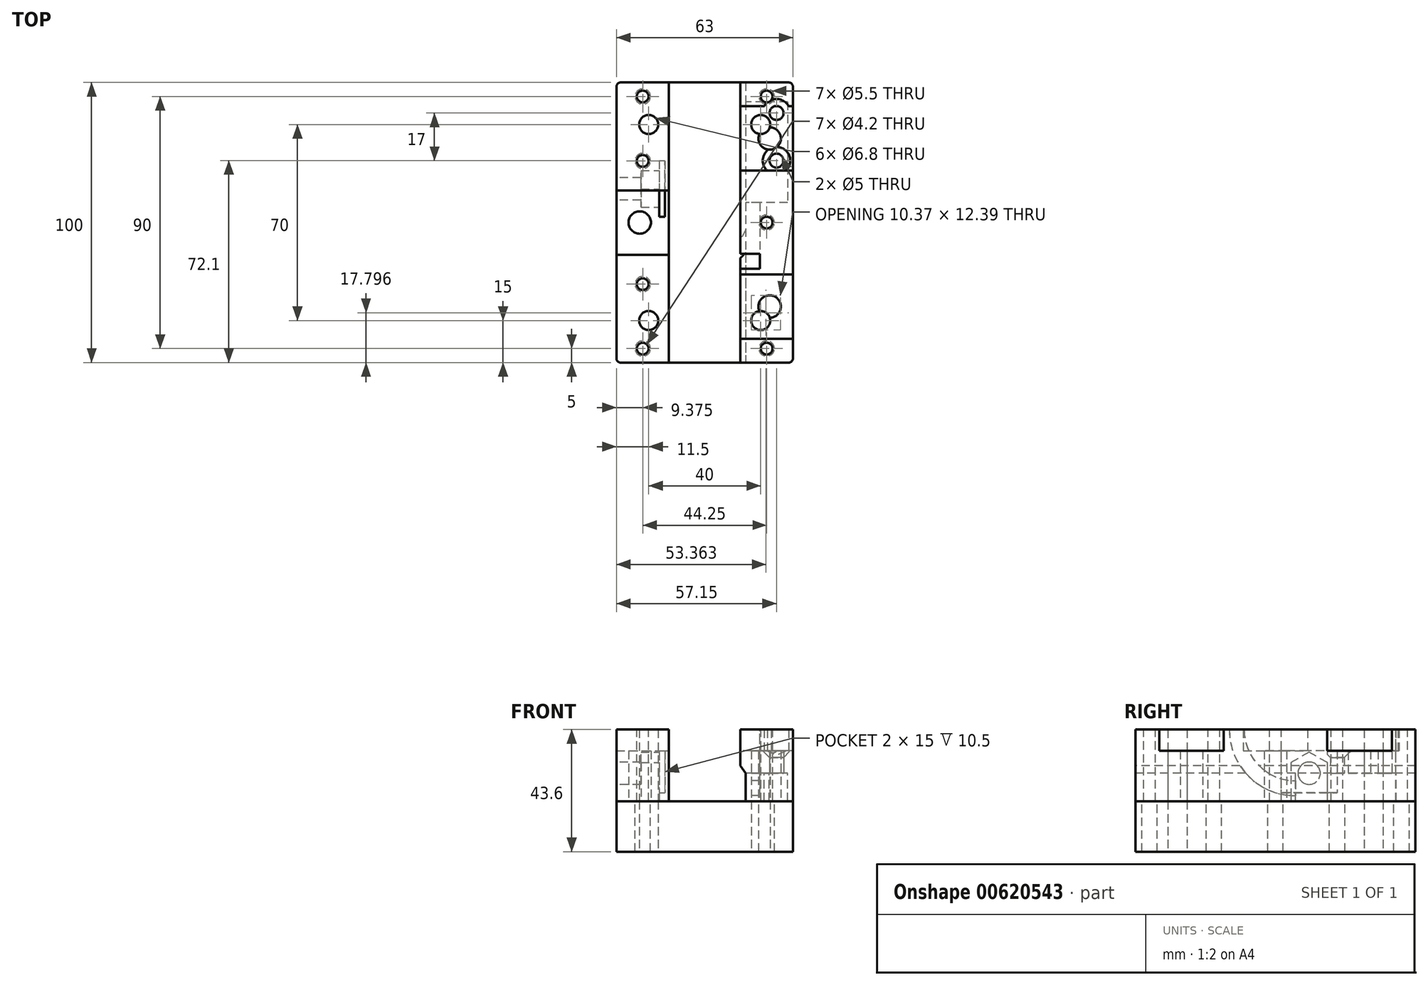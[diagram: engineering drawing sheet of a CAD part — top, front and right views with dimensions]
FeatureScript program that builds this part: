
annotation { "Feature Type Name" : "Feature", "Feature Type Description" : "" }
export const myFeature = defineFeature(function(context is Context, id is Id, definition is map)
    precondition{}
    {
        {
            var Q0;
            Q0=qCreatedBy(makeId("Top.planeOp"),FACE);
            var sketch = newSketch(context, id + "F0", { "sketchPlane" : qUnion([Q0])});
            skLineSegment(sketch, "E0.bottom", {"start": v(31.5, 50) * mm, "end": v(-31.5, 50) * mm});
            skLineSegment(sketch, "E0.top", {"start": v(31.5, -50) * mm, "end": v(-31.5, -50) * mm});
            skLineSegment(sketch, "E0.left", {"start": v(31.5, 50) * mm, "end": v(31.5, -50) * mm});
            skLineSegment(sketch, "E0.right", {"start": v(-31.5, 50) * mm, "end": v(-31.5, -50) * mm});
            skPoint(sketch, "E0.middle", {"position": v(0, 0) * mm});
            skCircle(sketch, "E1", {"center": v(-23.2, 0) * mm, "radius": 4 * mm});
            skCircle(sketch, "E2", {"center": v(23.2, 30) * mm, "radius": 4 * mm});
            skCircle(sketch, "E3", {"center": v(23.2, -30) * mm, "radius": 4 * mm});
            skSolve(sketch);
        }
        {
            var Q0;
            Q0 = qSketchRegion(id + "F0", true);
            extrude(context, id + "F1", {"entities" : qUnion([Q0]), "depth" : 25.6 * mm, "offsetDistance" : 25 * mm});
        }
        {
            var Q0;
            Q0=qCreatedBy(makeId("Right.planeOp"),FACE);
            var sketch = newSketch(context, id + "F2", { "sketchPlane" : qUnion([Q0])});
            skLineSegment(sketch, "E4.bottom", {"start": v(-11.5, 25.6) * mm, "end": v(11.5, 25.6) * mm});
            skLineSegment(sketch, "E4.top", {"start": v(-11.5, 18) * mm, "end": v(11.5, 18) * mm});
            skLineSegment(sketch, "E4.left", {"start": v(-11.5, 25.6) * mm, "end": v(-11.5, 18) * mm});
            skLineSegment(sketch, "E4.right", {"start": v(11.5, 25.6) * mm, "end": v(11.5, 18) * mm});
            skLineSegment(sketch, "E5.0", {"start": v(50, 25.6) * mm, "end": v(-50, 25.6) * mm});
            skPoint(sketch, "E6.0", {"position": v(0, 25.6) * mm});
            skSolve(sketch);
        }
        {
            var Q0;
            Q0 = qSketchRegion(id + "F2", true);
            extrude(context, id + "F3", {"entities" : qUnion([Q0]), "operationType" : NewBodyOperationType.REMOVE, "endBound" : BoundingType.THROUGH_ALL, "oppositeDirection" : true, "depth" : 25 * mm, "offsetDistance" : 25 * mm});
        }
        {
            var Q0;
            Q0=qCreatedBy(makeId("Right.planeOp"),FACE);
            var sketch = newSketch(context, id + "F4", { "sketchPlane" : qUnion([Q0])});
            skLineSegment(sketch, "E7.bottom", {"start": v(-18.5, 25.6) * mm, "end": v(-41.5, 25.6) * mm});
            skLineSegment(sketch, "E7.top", {"start": v(-18.5, 18) * mm, "end": v(-41.5, 18) * mm});
            skLineSegment(sketch, "E7.left", {"start": v(-18.5, 25.6) * mm, "end": v(-18.5, 18) * mm});
            skLineSegment(sketch, "E7.right", {"start": v(-41.5, 25.6) * mm, "end": v(-41.5, 18) * mm});
            skPoint(sketch, "E7.middle", {"position": v(-30, 21.8) * mm});
            skLineSegment(sketch, "E8.bottom", {"start": v(41.5, 25.6) * mm, "end": v(18.5, 25.6) * mm});
            skLineSegment(sketch, "E8.top", {"start": v(41.5, 18) * mm, "end": v(18.5, 18) * mm});
            skLineSegment(sketch, "E8.left", {"start": v(41.5, 25.6) * mm, "end": v(41.5, 18) * mm});
            skLineSegment(sketch, "E8.right", {"start": v(18.5, 25.6) * mm, "end": v(18.5, 18) * mm});
            skPoint(sketch, "E8.middle", {"position": v(30, 21.8) * mm});
            skLineSegment(sketch, "E9.0", {"start": v(50, 25.6) * mm, "end": v(-50, 25.6) * mm});
            skSolve(sketch);
        }
        {
            var Q0;
            Q0 = qSketchRegion(id + "F4", true);
            extrude(context, id + "F5", {"entities" : qUnion([Q0]), "operationType" : NewBodyOperationType.REMOVE, "endBound" : BoundingType.THROUGH_ALL, "depth" : 25 * mm, "offsetDistance" : 25 * mm});
        }
        {
            var Q0;
            Q0=makeQuery(id+"F1.opExtrude","CAP_FACE",FACE,{"disambiguationData":[OSD([sQuery(id+"F0.wireOp",EDGE,"E0.bottom"),sQuery(id+"F0.wireOp",EDGE,"E0.top"),sQuery(id+"F0.wireOp",EDGE,"E0.left"),sQuery(id+"F0.wireOp",EDGE,"E0.right"),sQuery(id+"F0.wireOp",EDGE,"E1"),sQuery(id+"F0.wireOp",EDGE,"E2"),sQuery(id+"F0.wireOp",EDGE,"E3")])],"isStart":true});
            var sketch = newSketch(context, id + "F6", { "sketchPlane" : qUnion([Q0])});
            skLineSegment(sketch, "E10.bottom", {"start": v(12.75, 50) * mm, "end": v(-12.75, 50) * mm});
            skLineSegment(sketch, "E10.top", {"start": v(12.75, -50) * mm, "end": v(-12.75, -50) * mm});
            skLineSegment(sketch, "E10.left", {"start": v(12.75, 50) * mm, "end": v(12.75, -50) * mm});
            skLineSegment(sketch, "E10.right", {"start": v(-12.75, 50) * mm, "end": v(-12.75, -50) * mm});
            skPoint(sketch, "E10.middle", {"position": v(0, 0) * mm});
            skSolve(sketch);
        }
        {
            var Q0;
            Q0 = qSketchRegion(id + "F6", true);
            extrude(context, id + "F7", {"entities" : qUnion([Q0]), "operationType" : NewBodyOperationType.REMOVE, "endBound" : BoundingType.THROUGH_ALL, "oppositeDirection" : true, "depth" : 25.2 * mm, "offsetDistance" : 25 * mm});
        }
        {
            var Q0;
            Q0=makeQuery(id+"F1.opExtrude","SWEPT_FACE",FACE,{"disambiguationData":[OSD([sQuery(id+"F0.wireOp",EDGE,"E0.right")])]});
            var sketch = newSketch(context, id + "F8", { "sketchPlane" : qUnion([Q0])});
            skCircle(sketch, "E11", {"center": v(-12, 10) * mm, "radius": 4 * mm});
            skSolve(sketch);
        }
        {
            var Q0;
            Q0 = qSketchRegion(id + "F8", true);
            extrude(context, id + "F9", {"entities" : qUnion([Q0]), "operationType" : NewBodyOperationType.REMOVE, "oppositeDirection" : true, "depth" : 17 * mm, "offsetDistance" : 25 * mm});
        }
        {
            var Q0;
            {var subQ0=sQuery(id+"F0.wireOp",EDGE,"E0.top");var subQ1=sQuery(id+"F0.wireOp",EDGE,"E0.left");Q0=makeQuery(id+"F7.boolean.opBoolean","SPLIT",FACE,{"disambiguationData":[TD([makeQuery(id+"F5.boolean.opBoolean","COPY",FACE,{"derivedFrom":makeQuery(id+"F5.opExtrude","SWEPT_FACE",FACE,{"disambiguationData":[OSD([sQuery(id+"F4.wireOp",EDGE,"E7.right")])]})})])],"derivedFrom":makeQuery(id+"F1.opExtrude","CAP_FACE",FACE,{"disambiguationData":[OSD([sQuery(id+"F0.wireOp",EDGE,"E0.bottom"),subQ0,subQ1,sQuery(id+"F0.wireOp",EDGE,"E0.right"),sQuery(id+"F0.wireOp",EDGE,"E1"),sQuery(id+"F0.wireOp",EDGE,"E2"),sQuery(id+"F0.wireOp",EDGE,"E3")])],"isStart":false})});}
            var sketch = newSketch(context, id + "F10", { "sketchPlane" : qUnion([Q0])});
            skCircle(sketch, "E12", {"center": v(22.12, -45) * mm, "radius": 2.1 * mm});
            skPoint(sketch, "E12.centerSnap0", {"position": v(22.12, -50) * mm});
            skCircle(sketch, "E13", {"center": v(-22.13, -45) * mm, "radius": 2.1 * mm});
            skCircle(sketch, "E14", {"center": v(22.12, 0) * mm, "radius": 2.1 * mm});
            skCircle(sketch, "E15", {"center": v(-22.13, -22) * mm, "radius": 2.1 * mm});
            skCircle(sketch, "E16.MirrorC", {"center": v(-22.13, 22) * mm, "radius": 2.1 * mm});
            skCircle(sketch, "E17.MirrorC", {"center": v(-22.13, 45) * mm, "radius": 2.1 * mm});
            skCircle(sketch, "E18.MirrorC", {"center": v(22.12, 45) * mm, "radius": 2.1 * mm});
            skSolve(sketch);
        }
        {
            var Q0;
            Q0 = qSketchRegion(id + "F10", true);
            extrude(context, id + "F11", {"entities" : qUnion([Q0]), "operationType" : NewBodyOperationType.REMOVE, "oppositeDirection" : true, "depth" : 29 * mm, "offsetDistance" : 25 * mm});
        }
        {
            var Q0;
            {var subQ4=sQuery(id+"F0.wireOp",EDGE,"E0.left");var subQ5=sQuery(id+"F0.wireOp",EDGE,"E0.top");Q0=makeQuery(id+"F7.boolean.opBoolean","SPLIT",FACE,{"disambiguationData":[TD([makeQuery(id+"F1.opExtrude","SWEPT_FACE",FACE,{"disambiguationData":[OSD([subQ4])]})])],"derivedFrom":makeQuery(id+"F1.opExtrude","SWEPT_FACE",FACE,{"disambiguationData":[OSD([subQ5])]})});}
            var sketch = newSketch(context, id + "F12", { "sketchPlane" : qUnion([Q0])});
            skLineSegment(sketch, "E19", {"start": v(12.75, 0) * mm, "end": v(12.75, 12.71) * mm});
            skLineSegment(sketch, "E20", {"start": v(12.75, 12.71) * mm, "end": v(14.65, 10) * mm});
            skLineSegment(sketch, "E21", {"start": v(14.65, 10) * mm, "end": v(14.65, 0) * mm});
            skLineSegment(sketch, "E22", {"start": v(14.65, 0) * mm, "end": v(12.75, 0) * mm});
            skSolve(sketch);
        }
        {
            var Q0;
            Q0 = qSketchRegion(id + "F12", true);
            extrude(context, id + "F13", {"entities" : qUnion([Q0]), "operationType" : NewBodyOperationType.REMOVE, "endBound" : BoundingType.THROUGH_ALL, "oppositeDirection" : true, "depth" : 25 * mm, "offsetDistance" : 25 * mm});
        }
        {
            var Q0;
            Q0=makeQuery(id+"F13.boolean.opBoolean","COPY",FACE,{"derivedFrom":makeQuery(id+"F13.opExtrude","SWEPT_FACE",FACE,{"disambiguationData":[OSD([sQuery(id+"F12.wireOp",EDGE,"E21")])]})});
            var sketch = newSketch(context, id + "F14", { "sketchPlane" : qUnion([Q0])});
            skLineSegment(sketch, "E23.bottom", {"start": v(-7.1, 0) * mm, "end": v(-43.1, 0) * mm});
            skLineSegment(sketch, "E23.top", {"start": v(-7.1, 10) * mm, "end": v(-43.1, 10) * mm});
            skLineSegment(sketch, "E23.left", {"start": v(-7.1, 0) * mm, "end": v(-7.1, 10) * mm});
            skLineSegment(sketch, "E23.right", {"start": v(-43.1, 0) * mm, "end": v(-43.1, 10) * mm});
            skArc(sketch, "E24", {"start": v(-7.1, 7.3) * mm, "mid": v(5.84, 12.66) * mm, "end": v(11.2, 25.6) * mm});
            skArc(sketch, "E25.0", {"start": v(-7.1, 2) * mm, "mid": v(9.59, 8.91) * mm, "end": v(16.5, 25.6) * mm});
            skLineSegment(sketch, "E26.trimOffspring", {"start": v(11.2, 25.6) * mm, "end": v(18.5, 25.6) * mm});
            skPoint(sketch, "E27.0.start.orphan", {"position": v(-18.5, 25.6) * mm});
            skLineSegment(sketch, "E28", {"start": v(-18.5, 25.6) * mm, "end": v(18.5, 25.6) * mm, "construction": true});
            skSolve(sketch);
        }
        {
            var Q0;
            {var subQ3=sQuery(id+"F14.wireOp",EDGE,"E23.bottom");Q0=makeQuery(id+"F14.imprint","IMPRINT",FACE,{"disambiguationData":[TD([[makeQuery(id+"F14.imprint","IMPRINT",EDGE,{"derivedFrom":subQ3}),1.0]])]});}
            extrude(context, id + "F15", {"entities" : qUnion([Q0]), "operationType" : NewBodyOperationType.REMOVE, "oppositeDirection" : true, "depth" : 15 * mm, "offsetDistance" : 25 * mm});
        }
        {
            var Q0;
            Q0 = qSketchRegion(id + "F14", true);
            extrude(context, id + "F16", {"entities" : qUnion([Q0]), "operationType" : NewBodyOperationType.REMOVE, "oppositeDirection" : true, "depth" : 10 * mm, "offsetDistance" : 25 * mm, "symmetric" : true});
        }
        {
            var Q0;
            Q0=makeQuery(id+"F15.boolean.opBoolean","COPY",FACE,{"derivedFrom":makeQuery(id+"F15.opExtrude","SWEPT_FACE",FACE,{"disambiguationData":[OSD([sQuery(id+"F14.wireOp",EDGE,"E23.top")])]})});
            var sketch = newSketch(context, id + "F17", { "sketchPlane" : qUnion([Q0])});
            skLineSegment(sketch, "E29.0", {"start": v(14.65, -7.1) * mm, "end": v(14.65, -43.1) * mm});
            skLineSegment(sketch, "E30.0", {"start": v(29.65, -43.1) * mm, "end": v(23.02, -43.1) * mm});
            skCircle(sketch, "E31", {"center": v(25.65, -39.1) * mm, "radius": 2.5 * mm});
            skCircle(sketch, "E32", {"center": v(25.65, -22.1) * mm, "radius": 2.5 * mm});
            skSolve(sketch);
        }
        {
            var Q0;
            Q0 = qSketchRegion(id + "F17", true);
            extrude(context, id + "F18", {"entities" : qUnion([Q0]), "operationType" : NewBodyOperationType.REMOVE, "endBound" : BoundingType.THROUGH_ALL, "oppositeDirection" : true, "depth" : 25 * mm, "offsetDistance" : 25 * mm});
        }
        {
            var Q0;
            Q0=makeQuery(id+"F5.boolean.opBoolean","COPY",FACE,{"derivedFrom":makeQuery(id+"F5.opExtrude","SWEPT_FACE",FACE,{"disambiguationData":[OSD([sQuery(id+"F4.wireOp",EDGE,"E8.top")])]})});
            var sketch = newSketch(context, id + "F19", { "sketchPlane" : qUnion([Q0])});
            skCircle(sketch, "E33.0", {"center": v(25.65, 39.1) * mm, "radius": 2.5 * mm});
            skCircle(sketch, "E33.1", {"center": v(25.65, 22.1) * mm, "radius": 2.5 * mm});
            skCircle(sketch, "E34.0", {"center": v(25.65, 39.1) * mm, "radius": 5 * mm});
            skCircle(sketch, "E35.0", {"center": v(25.65, 22.1) * mm, "radius": 5 * mm});
            skLineSegment(sketch, "E36.0", {"start": v(17.75, 36.5) * mm, "end": v(17.75, 23.5) * mm});
            skLineSegment(sketch, "E36.1", {"start": v(26.5, 36.5) * mm, "end": v(17.75, 36.5) * mm});
            skLineSegment(sketch, "E36.2", {"start": v(26.5, 23.5) * mm, "end": v(26.5, 36.5) * mm});
            skLineSegment(sketch, "E36.3", {"start": v(17.75, 23.5) * mm, "end": v(26.5, 23.5) * mm});
            skSolve(sketch);
        }
        {
            var Q0;
            {var subQ0=sQuery(id+"F19.wireOp",EDGE,"E34.0");var subQ1=makeQuery(id+"F5.boolean.opBoolean","COPY",EDGE,{"derivedFrom":makeQuery(id+"F5.opExtrude","SWEPT_EDGE",EDGE,{"disambiguationData":[OSD([sQuery(id+"F4.wireOp",EDGE,"E8.top"),sQuery(id+"F4.wireOp",EDGE,"E8.left")])]})});var subQ2=makeQuery(id+"F19.imprint","INTERSECT",VERTEX,{"disambiguationData":[OD(0.0)],"derivedFrom":[subQ1,subQ0]});Q0=makeQuery(id+"F19.imprint","IMPRINT",FACE,{"disambiguationData":[TD([[makeQuery(id+"F19.imprint","IMPRINT",EDGE,{"disambiguationData":[TD([[subQ2,1.0]])],"derivedFrom":subQ0}),1.0]])]});}
            var Q1;
            {var subQ0=sQuery(id+"F19.wireOp",EDGE,"E35.0");var subQ1=makeQuery(id+"F5.boolean.opBoolean","COPY",EDGE,{"derivedFrom":makeQuery(id+"F5.opExtrude","SWEPT_EDGE",EDGE,{"disambiguationData":[OSD([sQuery(id+"F4.wireOp",EDGE,"E8.top"),sQuery(id+"F4.wireOp",EDGE,"E8.right")])]})});var subQ2=makeQuery(id+"F19.imprint","INTERSECT",VERTEX,{"disambiguationData":[OD(0.0)],"derivedFrom":[subQ1,subQ0]});Q1=makeQuery(id+"F19.imprint","IMPRINT",FACE,{"disambiguationData":[TD([[makeQuery(id+"F19.imprint","IMPRINT",EDGE,{"disambiguationData":[TD([[subQ2,-1.0]])],"derivedFrom":subQ0}),1.0]])]});}
            var Q2;
            {var subQ0=sQuery(id+"F0.wireOp",EDGE,"E0.left");Q2=makeQuery(id+"F7.boolean.opBoolean","SPLIT",FACE,{"disambiguationData":[TD([makeQuery(id+"F5.boolean.opBoolean","COPY",FACE,{"derivedFrom":makeQuery(id+"F5.opExtrude","SWEPT_FACE",FACE,{"disambiguationData":[OSD([sQuery(id+"F4.wireOp",EDGE,"E7.left")])]})})])],"derivedFrom":makeQuery(id+"F1.opExtrude","CAP_FACE",FACE,{"disambiguationData":[OSD([sQuery(id+"F0.wireOp",EDGE,"E0.bottom"),sQuery(id+"F0.wireOp",EDGE,"E0.top"),subQ0,sQuery(id+"F0.wireOp",EDGE,"E0.right"),sQuery(id+"F0.wireOp",EDGE,"E1"),sQuery(id+"F0.wireOp",EDGE,"E2"),sQuery(id+"F0.wireOp",EDGE,"E3")])],"isStart":false})});}
            extrude(context, id + "F20", {"entities" : qUnion([Q0, Q1]), "operationType" : NewBodyOperationType.REMOVE, "endBound" : BoundingType.UP_TO_SURFACE, "depth" : 25 * mm, "endBoundEntityFace" : qUnion([Q2]), "offsetDistance" : 25 * mm});
        }
        {
            var Q0;
            Q0=makeQuery(id+"F18.boolean.opBoolean","INTERSECT",EDGE,{"derivedFrom":[makeQuery(id+"F5.boolean.opBoolean","COPY",FACE,{"derivedFrom":makeQuery(id+"F5.opExtrude","SWEPT_FACE",FACE,{"disambiguationData":[OSD([sQuery(id+"F4.wireOp",EDGE,"E8.top")])]})}),makeQuery(id+"F18.opExtrude","SWEPT_FACE",FACE,{"disambiguationData":[OSD([sQuery(id+"F17.wireOp",EDGE,"E32")])]})]});
            var Q1;
            Q1=makeQuery(id+"F18.boolean.opBoolean","INTERSECT",EDGE,{"derivedFrom":[makeQuery(id+"F5.boolean.opBoolean","COPY",FACE,{"derivedFrom":makeQuery(id+"F5.opExtrude","SWEPT_FACE",FACE,{"disambiguationData":[OSD([sQuery(id+"F4.wireOp",EDGE,"E8.top")])]})}),makeQuery(id+"F18.opExtrude","SWEPT_FACE",FACE,{"disambiguationData":[OSD([sQuery(id+"F17.wireOp",EDGE,"E31")])]})]});
            chamfer(context, id + "F21", {"entities" : qUnion([Q0, Q1]), "width" : 2.4 * mm, "tangentPropagation" : true});
        }
        {
            var Q0;
            Q0=makeQuery(id+"F1.opExtrude","SWEPT_EDGE",EDGE,{"disambiguationData":[OSD([sQuery(id+"F0.wireOp",EDGE,"E0.bottom"),sQuery(id+"F0.wireOp",EDGE,"E0.right")])]});
            var Q1;
            Q1=makeQuery(id+"F1.opExtrude","SWEPT_EDGE",EDGE,{"disambiguationData":[OSD([sQuery(id+"F0.wireOp",EDGE,"E0.bottom"),sQuery(id+"F0.wireOp",EDGE,"E0.left")])]});
            var Q2;
            Q2=makeQuery(id+"F1.opExtrude","SWEPT_EDGE",EDGE,{"disambiguationData":[OSD([sQuery(id+"F0.wireOp",EDGE,"E0.top"),sQuery(id+"F0.wireOp",EDGE,"E0.left")])]});
            var Q3;
            Q3=makeQuery(id+"F1.opExtrude","SWEPT_EDGE",EDGE,{"disambiguationData":[OSD([sQuery(id+"F0.wireOp",EDGE,"E0.top"),sQuery(id+"F0.wireOp",EDGE,"E0.right")])]});
            fillet(context, id + "F22", {"entities" : qUnion([Q0, Q1, Q2, Q3]), "radius" : 1.5 * mm, "tangentPropagation" : true, "allowEdgeOverflow" : false});
        }
        {
            var Q0;
            {var subQ0=sQuery(id+"F0.wireOp",EDGE,"E1");var subQ1=sQuery(id+"F0.wireOp",EDGE,"E0.top");var subQ2=sQuery(id+"F0.wireOp",EDGE,"E0.right");var subQ3=sQuery(id+"F0.wireOp",EDGE,"E0.bottom");Q0=makeQuery(id+"F7.boolean.opBoolean","SPLIT",FACE,{"disambiguationData":[TD([makeQuery(id+"F1.opExtrude","SWEPT_FACE",FACE,{"disambiguationData":[OSD([subQ2])]})])],"derivedFrom":makeQuery(id+"F1.opExtrude","CAP_FACE",FACE,{"disambiguationData":[OSD([subQ3,subQ1,sQuery(id+"F0.wireOp",EDGE,"E0.left"),subQ2,subQ0,sQuery(id+"F0.wireOp",EDGE,"E2"),sQuery(id+"F0.wireOp",EDGE,"E3")])],"isStart":true})});}
            var sketch = newSketch(context, id + "F23", { "sketchPlane" : qUnion([Q0])});
            skLineSegment(sketch, "E37.bottom", {"start": v(-16.25, -2) * mm, "end": v(-14.25, -2) * mm});
            skLineSegment(sketch, "E37.top", {"start": v(-16.25, -22) * mm, "end": v(-14.25, -22) * mm});
            skLineSegment(sketch, "E37.left", {"start": v(-16.25, -2) * mm, "end": v(-16.25, -22) * mm});
            skLineSegment(sketch, "E37.right", {"start": v(-14.25, -2) * mm, "end": v(-14.25, -22) * mm});
            skLineSegment(sketch, "E38.0", {"start": v(-31.5, -16) * mm, "end": v(-31.5, -8) * mm, "construction": true});
            skLineSegment(sketch, "E39", {"start": v(-31.5, -12) * mm, "end": v(-16.25, -12) * mm, "construction": true});
            skSolve(sketch);
        }
        {
            var Q0;
            Q0 = qSketchRegion(id + "F23", true);
            var Q1;
            Q1=makeQuery(id+"F3.boolean.opBoolean","COPY",FACE,{"derivedFrom":makeQuery(id+"F3.opExtrude","SWEPT_FACE",FACE,{"disambiguationData":[OSD([sQuery(id+"F2.wireOp",EDGE,"E4.top")])]})});
            extrude(context, id + "F24", {"entities" : qUnion([Q0]), "operationType" : NewBodyOperationType.REMOVE, "endBound" : BoundingType.UP_TO_SURFACE, "oppositeDirection" : true, "depth" : 19 * mm, "endBoundEntityFace" : qUnion([Q1]), "offsetDistance" : 25 * mm});
        }
        {
            var Q0;
            Q0=makeQuery(id+"F24.boolean.opBoolean","COPY",FACE,{"derivedFrom":makeQuery(id+"F24.opExtrude","SWEPT_FACE",FACE,{"disambiguationData":[OSD([sQuery(id+"F23.wireOp",EDGE,"E37.left")])]})});
            var sketch = newSketch(context, id + "F25", { "sketchPlane" : qUnion([Q0])});
            skCircle(sketch, "E40.0", {"center": v(12, 10) * mm, "radius": 4 * mm, "construction": true});
            skLineSegment(sketch, "E41.0", {"start": v(2, 0) * mm, "end": v(22, 0) * mm});
            skCircle(sketch, "E42.cCircle", {"center": v(12, 10) * mm, "radius": 6.55 * mm, "construction": true});
            skLineSegment(sketch, "E42.0", {"start": v(12, 17.56) * mm, "end": v(5.45, 13.78) * mm});
            skLineSegment(sketch, "E42.1", {"start": v(18.55, 13.78) * mm, "end": v(12, 17.56) * mm});
            skLineSegment(sketch, "E42.2", {"start": v(18.55, 6.22) * mm, "end": v(18.55, 13.78) * mm, "construction": true});
            skLineSegment(sketch, "E42.3", {"start": v(12, 2.44) * mm, "end": v(18.55, 6.22) * mm, "construction": true});
            skLineSegment(sketch, "E42.4", {"start": v(5.45, 6.22) * mm, "end": v(12, 2.44) * mm, "construction": true});
            skLineSegment(sketch, "E42.5", {"start": v(5.45, 13.78) * mm, "end": v(5.45, 6.22) * mm});
            skPoint(sketch, "E42.0.midPoint", {"position": v(8.73, 15.67) * mm});
            skLineSegment(sketch, "E43", {"start": v(5.45, 6.22) * mm, "end": v(5.45, 0) * mm});
            skLineSegment(sketch, "E44", {"start": v(5.45, 0) * mm, "end": v(18.55, 0) * mm});
            skLineSegment(sketch, "E45", {"start": v(18.55, 0) * mm, "end": v(18.55, 13.78) * mm});
            skSolve(sketch);
        }
        {
            var Q0;
            Q0 = qSketchRegion(id + "F25", true);
            extrude(context, id + "F26", {"entities" : qUnion([Q0]), "operationType" : NewBodyOperationType.REMOVE, "oppositeDirection" : true, "depth" : 6.5 * mm, "offsetDistance" : 25 * mm});
        }
        {
            var Q0;
            {var subQ0=sQuery(id+"F0.wireOp",EDGE,"E1");var subQ1=sQuery(id+"F0.wireOp",EDGE,"E0.top");var subQ2=sQuery(id+"F0.wireOp",EDGE,"E0.right");var subQ3=sQuery(id+"F0.wireOp",EDGE,"E0.bottom");Q0=makeQuery(id+"F7.boolean.opBoolean","SPLIT",FACE,{"disambiguationData":[TD([makeQuery(id+"F1.opExtrude","SWEPT_FACE",FACE,{"disambiguationData":[OSD([subQ2])]})])],"derivedFrom":makeQuery(id+"F1.opExtrude","CAP_FACE",FACE,{"disambiguationData":[OSD([subQ3,subQ1,sQuery(id+"F0.wireOp",EDGE,"E0.left"),subQ2,subQ0,sQuery(id+"F0.wireOp",EDGE,"E2"),sQuery(id+"F0.wireOp",EDGE,"E3")])],"isStart":true})});}
            var sketch = newSketch(context, id + "F27", { "sketchPlane" : qUnion([Q0])});
            skLineSegment(sketch, "E46.bottom", {"start": v(-16.25, -22) * mm, "end": v(-14.25, -22) * mm});
            skLineSegment(sketch, "E46.top", {"start": v(-16.25, -2) * mm, "end": v(-14.25, -2) * mm});
            skLineSegment(sketch, "E46.left", {"start": v(-16.25, -22) * mm, "end": v(-16.25, -2) * mm});
            skLineSegment(sketch, "E46.right", {"start": v(-14.25, -22) * mm, "end": v(-14.25, -2) * mm});
            skSolve(sketch);
        }
        {
            var Q0;
            Q0 = qSketchRegion(id + "F27", true);
            extrude(context, id + "F28", {"entities" : qUnion([Q0]), "operationType" : NewBodyOperationType.ADD, "oppositeDirection" : true, "depth" : 3 * mm, "offsetDistance" : 25 * mm});
        }
        {
            var Q0;
            {var subQ0=sQuery(id+"F0.wireOp",EDGE,"E1");var subQ1=sQuery(id+"F0.wireOp",EDGE,"E0.top");var subQ2=sQuery(id+"F0.wireOp",EDGE,"E0.right");var subQ3=sQuery(id+"F0.wireOp",EDGE,"E0.bottom");Q0=makeQuery(id+"F28.boolean.opBoolean","MERGE",FACE,{"derivedFrom":[makeQuery(id+"F7.boolean.opBoolean","SPLIT",FACE,{"disambiguationData":[TD([makeQuery(id+"F1.opExtrude","SWEPT_FACE",FACE,{"disambiguationData":[OSD([subQ2])]})])],"derivedFrom":makeQuery(id+"F1.opExtrude","CAP_FACE",FACE,{"disambiguationData":[OSD([subQ3,subQ1,sQuery(id+"F0.wireOp",EDGE,"E0.left"),subQ2,subQ0,sQuery(id+"F0.wireOp",EDGE,"E2"),sQuery(id+"F0.wireOp",EDGE,"E3")])],"isStart":true})}),makeQuery(id+"F28.opExtrude","CAP_FACE",FACE,{"disambiguationData":[OSD([sQuery(id+"F27.wireOp",EDGE,"E46.bottom"),sQuery(id+"F27.wireOp",EDGE,"E46.top"),sQuery(id+"F27.wireOp",EDGE,"E46.left"),sQuery(id+"F27.wireOp",EDGE,"E46.right")])],"isStart":true})]});}
            var sketch = newSketch(context, id + "F29", { "sketchPlane" : qUnion([Q0])});
            skLineSegment(sketch, "E47.0.0", {"start": v(31.5, -48.5) * mm, "end": v(31.5, 48.5) * mm});
            skArc(sketch, "E47.0.1", {"start": v(31.5, 48.5) * mm, "mid": v(31.06, 49.56) * mm, "end": v(30, 50) * mm});
            skLineSegment(sketch, "E47.0.2", {"start": v(30, 50) * mm, "end": v(14.65, 50) * mm});
            skLineSegment(sketch, "E47.0.8", {"start": v(14.65, -50) * mm, "end": v(30, -50) * mm});
            skArc(sketch, "E47.0.9", {"start": v(30, -50) * mm, "mid": v(31.06, -49.56) * mm, "end": v(31.5, -48.5) * mm});
            skLineSegment(sketch, "E48.0", {"start": v(-31.5, -48.5) * mm, "end": v(-31.5, 48.5) * mm});
            skLineSegment(sketch, "E49.0", {"start": v(-12.75, -50) * mm, "end": v(-30, -50) * mm});
            skPoint(sketch, "E49.1", {"position": v(-31.06, -49.56) * mm});
            skArc(sketch, "E50.0", {"start": v(-31.5, -48.5) * mm, "mid": v(-31.06, -49.56) * mm, "end": v(-30, -50) * mm});
            skLineSegment(sketch, "E51.0", {"start": v(-12.75, 50) * mm, "end": v(-30, 50) * mm});
            skArc(sketch, "E52.0", {"start": v(-30, 50) * mm, "mid": v(-31.06, 49.56) * mm, "end": v(-31.5, 48.5) * mm});
            skLineSegment(sketch, "E53", {"start": v(-30, 50) * mm, "end": v(30, 50) * mm});
            skLineSegment(sketch, "E54", {"start": v(30, -50) * mm, "end": v(-30, -50) * mm});
            skPoint(sketch, "E47.0.4.start.orphan", {"position": v(14.65, -7.1) * mm});
            skPoint(sketch, "E47.0.5.start.orphan", {"position": v(29.65, -7.1) * mm});
            skPoint(sketch, "E47.0.6.start.orphan", {"position": v(29.65, -43.1) * mm});
            skPoint(sketch, "E47.0.7.start.orphan", {"position": v(23.02, -43.1) * mm});
            skCircle(sketch, "E55.0", {"center": v(-22.13, 45) * mm, "radius": 2.1 * mm});
            skCircle(sketch, "E56.0", {"center": v(-22.13, 22) * mm, "radius": 2.1 * mm});
            skCircle(sketch, "E57.0", {"center": v(-22.13, -22) * mm, "radius": 2.1 * mm});
            skCircle(sketch, "E58.0", {"center": v(-22.13, -45) * mm, "radius": 2.1 * mm});
            skCircle(sketch, "E59.0", {"center": v(22.12, -45) * mm, "radius": 2.1 * mm});
            skCircle(sketch, "E60.0", {"center": v(22.12, 0) * mm, "radius": 2.1 * mm});
            skCircle(sketch, "E61.0", {"center": v(22.12, 45) * mm, "radius": 2.1 * mm});
            skCircle(sketch, "E62", {"center": v(-22.13, 22) * mm, "radius": 2.75 * mm});
            skCircle(sketch, "E63", {"center": v(-22.13, 45) * mm, "radius": 2.75 * mm});
            skCircle(sketch, "E64", {"center": v(22.12, 45) * mm, "radius": 2.75 * mm});
            skCircle(sketch, "E65", {"center": v(22.12, 0) * mm, "radius": 2.75 * mm});
            skCircle(sketch, "E66.MirrorC", {"center": v(-22.13, -22) * mm, "radius": 2.75 * mm});
            skCircle(sketch, "E67.MirrorC", {"center": v(-22.13, -45) * mm, "radius": 2.75 * mm});
            skCircle(sketch, "E68.MirrorC", {"center": v(22.12, -45) * mm, "radius": 2.75 * mm});
            skSolve(sketch);
        }
        {
            var Q0;
            Q0 = qSketchRegion(id + "F29", true);
            extrude(context, id + "F30", {"entities" : qUnion([Q0]), "depth" : 18 * mm, "offsetDistance" : 25 * mm});
        }
        {
            var Q0;
            Q0=makeQuery(id+"F30.opExtrude","CAP_FACE",FACE,{"disambiguationData":[OSD([sQuery(id+"F29.wireOp",EDGE,"E47.0.0"),sQuery(id+"F29.wireOp",EDGE,"E47.0.1"),sQuery(id+"F29.wireOp",EDGE,"E47.0.9"),sQuery(id+"F29.wireOp",EDGE,"E48.0"),sQuery(id+"F29.wireOp",EDGE,"E50.0"),sQuery(id+"F29.wireOp",EDGE,"E52.0"),sQuery(id+"F29.wireOp",EDGE,"E53"),sQuery(id+"F29.wireOp",EDGE,"E54"),sQuery(id+"F29.wireOp",EDGE,"E62"),sQuery(id+"F29.wireOp",EDGE,"E63"),sQuery(id+"F29.wireOp",EDGE,"E64"),sQuery(id+"F29.wireOp",EDGE,"E65"),sQuery(id+"F29.wireOp",EDGE,"E66.MirrorC"),sQuery(id+"F29.wireOp",EDGE,"E67.MirrorC"),sQuery(id+"F29.wireOp",EDGE,"E68.MirrorC")])],"isStart":false});
            var sketch = newSketch(context, id + "F31", { "sketchPlane" : qUnion([Q0])});
            skCircle(sketch, "E69", {"center": v(-20, 35) * mm, "radius": 3.4 * mm});
            skCircle(sketch, "E70", {"center": v(20, 35) * mm, "radius": 3.4 * mm});
            skCircle(sketch, "E71.MirrorC", {"center": v(20, -35) * mm, "radius": 3.4 * mm});
            skCircle(sketch, "E72.MirrorC", {"center": v(-20, -35) * mm, "radius": 3.4 * mm});
            skSolve(sketch);
        }
        {
            var Q0;
            Q0 = qSketchRegion(id + "F31", true);
            extrude(context, id + "F32", {"entities" : qUnion([Q0]), "operationType" : NewBodyOperationType.REMOVE, "endBound" : BoundingType.THROUGH_ALL, "oppositeDirection" : true, "depth" : 25 * mm, "offsetDistance" : 25 * mm});
        }
    });
